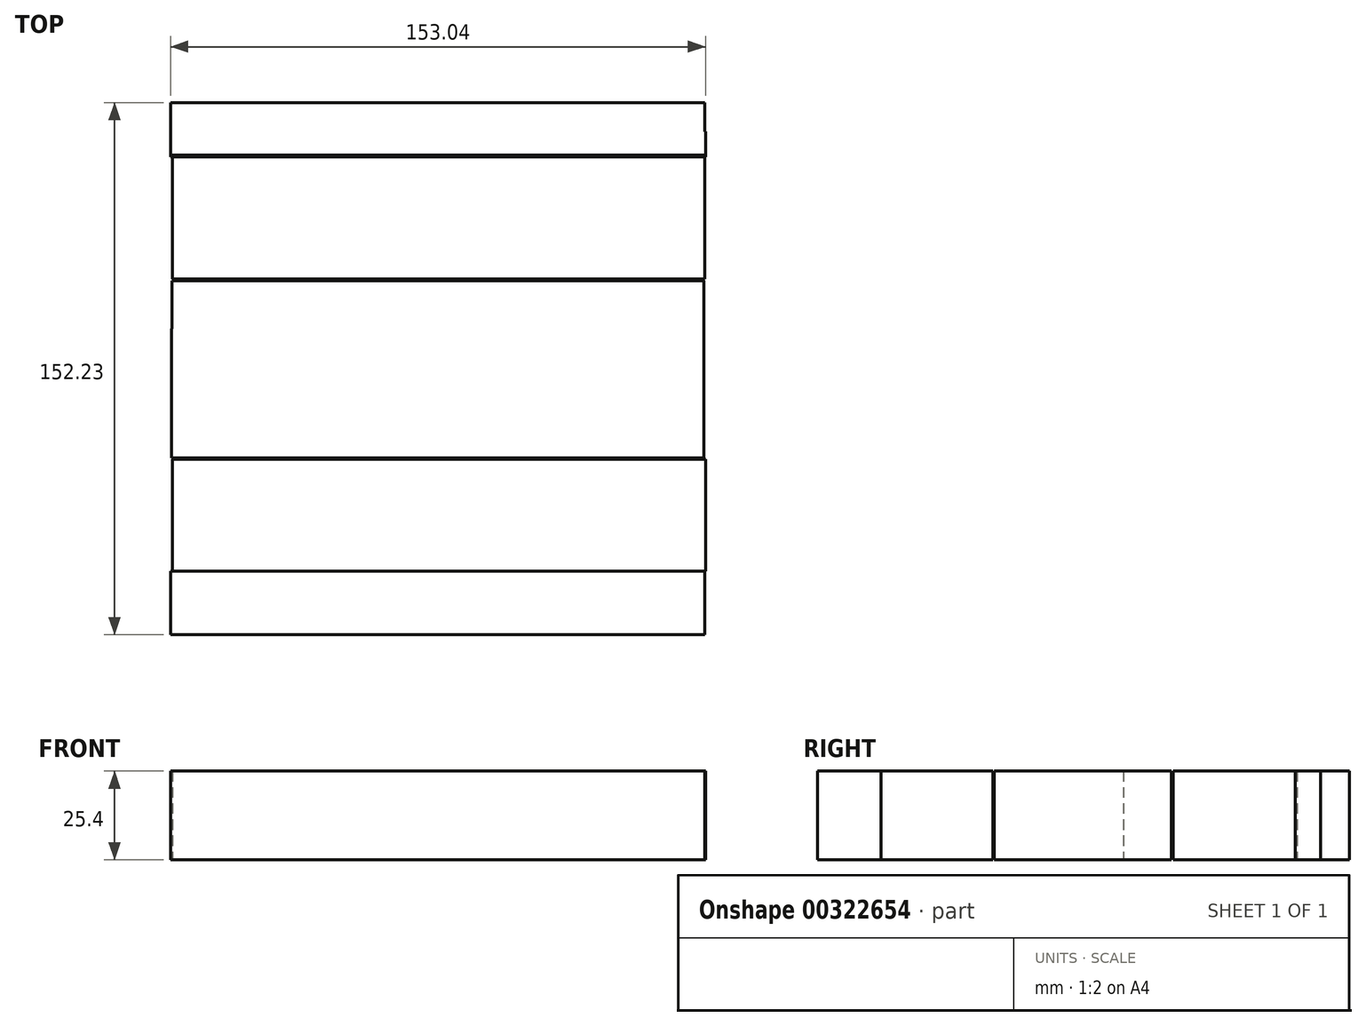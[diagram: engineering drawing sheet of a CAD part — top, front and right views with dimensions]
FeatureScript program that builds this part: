
annotation { "Feature Type Name" : "Feature", "Feature Type Description" : "" }
export const myFeature = defineFeature(function(context is Context, id is Id, definition is map)
    precondition{}
    {
        {
            var Q0;
            Q0=qCreatedBy(makeId("Top.planeOp"),FACE);
            var sketch = newSketch(context, id + "F0", { "sketchPlane" : qUnion([Q0])});
            skLineSegment(sketch, "E0.bottom", {"start": v(-76.6, 11.26) * mm, "end": v(75.75, 11.26) * mm});
            skLineSegment(sketch, "E0.top", {"start": v(-76.6, -11.48) * mm, "end": v(75.75, -11.48) * mm});
            skLineSegment(sketch, "E0.left", {"start": v(-76.6, 11.26) * mm, "end": v(-76.6, -11.48) * mm});
            skLineSegment(sketch, "E0.right", {"start": v(75.75, 11.26) * mm, "end": v(75.75, -11.48) * mm});
            skLineSegment(sketch, "E1.bottom", {"start": v(-76.46, 25.02) * mm, "end": v(75.75, 25.02) * mm});
            skLineSegment(sketch, "E1.top", {"start": v(-76.46, 11.26) * mm, "end": v(75.75, 11.26) * mm});
            skLineSegment(sketch, "E1.left", {"start": v(-76.46, 25.02) * mm, "end": v(-76.46, 11.26) * mm});
            skLineSegment(sketch, "E1.right", {"start": v(75.75, 25.02) * mm, "end": v(75.75, 11.26) * mm});
            skLineSegment(sketch, "E2.bottom", {"start": v(-76.46, 25.02) * mm, "end": v(-76.46, 25.02) * mm});
            skLineSegment(sketch, "E2.top", {"start": v(-76.46, 18.14) * mm, "end": v(-76.46, 18.14) * mm});
            skLineSegment(sketch, "E2.left", {"start": v(-76.46, 25.02) * mm, "end": v(-76.46, 18.14) * mm});
            skLineSegment(sketch, "E2.right", {"start": v(-76.46, 25.02) * mm, "end": v(-76.46, 18.14) * mm});
            skLineSegment(sketch, "E3.bottom", {"start": v(-76.6, -25.64) * mm, "end": v(75.75, -25.64) * mm});
            skLineSegment(sketch, "E3.left", {"start": v(-76.6, -25.64) * mm, "end": v(-76.6, -11.48) * mm});
            skLineSegment(sketch, "E3.right", {"start": v(75.75, -25.64) * mm, "end": v(75.75, -11.48) * mm});
            skSolve(sketch);
        }
        {
            var Q0;
            Q0 = qSketchRegion(id + "F0", true);
            extrude(context, id + "F1", {"entities" : qUnion([Q0]), "depth" : 25.4 * mm});
        }
        {
            var Q0;
            Q0=qCreatedBy(makeId("Top.planeOp"),FACE);
            var sketch = newSketch(context, id + "F2", { "sketchPlane" : qUnion([Q0])});
            skLineSegment(sketch, "E4.bottom", {"start": v(-76.31, 41.62) * mm, "end": v(75.92, 41.62) * mm});
            skLineSegment(sketch, "E4.top", {"start": v(-76.31, 25.5) * mm, "end": v(75.92, 25.5) * mm});
            skLineSegment(sketch, "E4.left", {"start": v(-76.31, 41.62) * mm, "end": v(-76.31, 25.5) * mm});
            skLineSegment(sketch, "E4.right", {"start": v(75.92, 41.62) * mm, "end": v(75.92, 25.5) * mm});
            skLineSegment(sketch, "E5.bottom", {"start": v(-76.31, -26.04) * mm, "end": v(76.19, -26.04) * mm});
            skLineSegment(sketch, "E5.top", {"start": v(-76.31, -43.76) * mm, "end": v(76.19, -43.76) * mm});
            skLineSegment(sketch, "E5.left", {"start": v(-76.31, -26.04) * mm, "end": v(-76.31, -43.76) * mm});
            skLineSegment(sketch, "E5.right", {"start": v(76.19, -26.04) * mm, "end": v(76.19, -43.76) * mm});
            skLineSegment(sketch, "E6.bottom", {"start": v(-76.31, -58) * mm, "end": v(76.19, -58) * mm});
            skLineSegment(sketch, "E6.left", {"start": v(-76.31, -58) * mm, "end": v(-76.31, -43.76) * mm});
            skLineSegment(sketch, "E6.right", {"start": v(76.19, -58) * mm, "end": v(76.19, -43.76) * mm});
            skLineSegment(sketch, "E7.bottom", {"start": v(-76.31, 60.95) * mm, "end": v(75.92, 60.95) * mm});
            skLineSegment(sketch, "E7.left", {"start": v(-76.31, 60.95) * mm, "end": v(-76.31, 41.62) * mm});
            skLineSegment(sketch, "E7.right", {"start": v(75.92, 60.95) * mm, "end": v(75.92, 41.62) * mm});
            skSolve(sketch);
        }
        {
            var Q0;
            Q0 = qSketchRegion(id + "F2", true);
            extrude(context, id + "F3", {"entities" : qUnion([Q0]), "depth" : 25.4 * mm});
        }
        {
            var Q0;
            Q0=makeQuery(id+"F2.imprint","IMPRINT",FACE,{"disambiguationData":[TD([[makeQuery(id+"F2.imprint","IMPRINT",EDGE,{"derivedFrom":sQuery(id+"F2.wireOp",EDGE,"E7.bottom")}),-1.0]])]});
            var sketch = newSketch(context, id + "F4", { "sketchPlane" : qUnion([Q0])});
            skLineSegment(sketch, "E8.bottom", {"start": v(-76.85, 67.66) * mm, "end": v(76.19, 67.66) * mm});
            skLineSegment(sketch, "E8.top", {"start": v(-76.85, 60.41) * mm, "end": v(76.19, 60.41) * mm});
            skLineSegment(sketch, "E8.left", {"start": v(-76.85, 67.66) * mm, "end": v(-76.85, 60.41) * mm});
            skLineSegment(sketch, "E8.right", {"start": v(76.19, 67.66) * mm, "end": v(76.19, 60.41) * mm});
            skLineSegment(sketch, "E9.bottom", {"start": v(-76.85, 60.41) * mm, "end": v(75.92, 60.41) * mm});
            skLineSegment(sketch, "E9.top", {"start": v(-76.85, 75.98) * mm, "end": v(75.92, 75.98) * mm});
            skLineSegment(sketch, "E9.left", {"start": v(-76.85, 60.41) * mm, "end": v(-76.85, 75.98) * mm});
            skLineSegment(sketch, "E9.right", {"start": v(75.92, 60.41) * mm, "end": v(75.92, 75.98) * mm});
            skLineSegment(sketch, "E10.bottom", {"start": v(-76.85, -64.7) * mm, "end": v(75.92, -64.7) * mm});
            skLineSegment(sketch, "E10.top", {"start": v(-76.85, -58) * mm, "end": v(75.92, -58) * mm});
            skLineSegment(sketch, "E10.left", {"start": v(-76.85, -64.7) * mm, "end": v(-76.85, -58) * mm});
            skLineSegment(sketch, "E10.right", {"start": v(75.92, -64.7) * mm, "end": v(75.92, -58) * mm});
            skLineSegment(sketch, "E11.bottom", {"start": v(-76.85, -76.25) * mm, "end": v(75.92, -76.25) * mm});
            skLineSegment(sketch, "E11.left", {"start": v(-76.85, -76.25) * mm, "end": v(-76.85, -64.7) * mm});
            skLineSegment(sketch, "E11.right", {"start": v(75.92, -76.25) * mm, "end": v(75.92, -64.7) * mm});
            skSolve(sketch);
        }
        {
            var Q0;
            Q0 = qSketchRegion(id + "F4", true);
            extrude(context, id + "F5", {"entities" : qUnion([Q0]), "depth" : 25.4 * mm});
        }
    });
